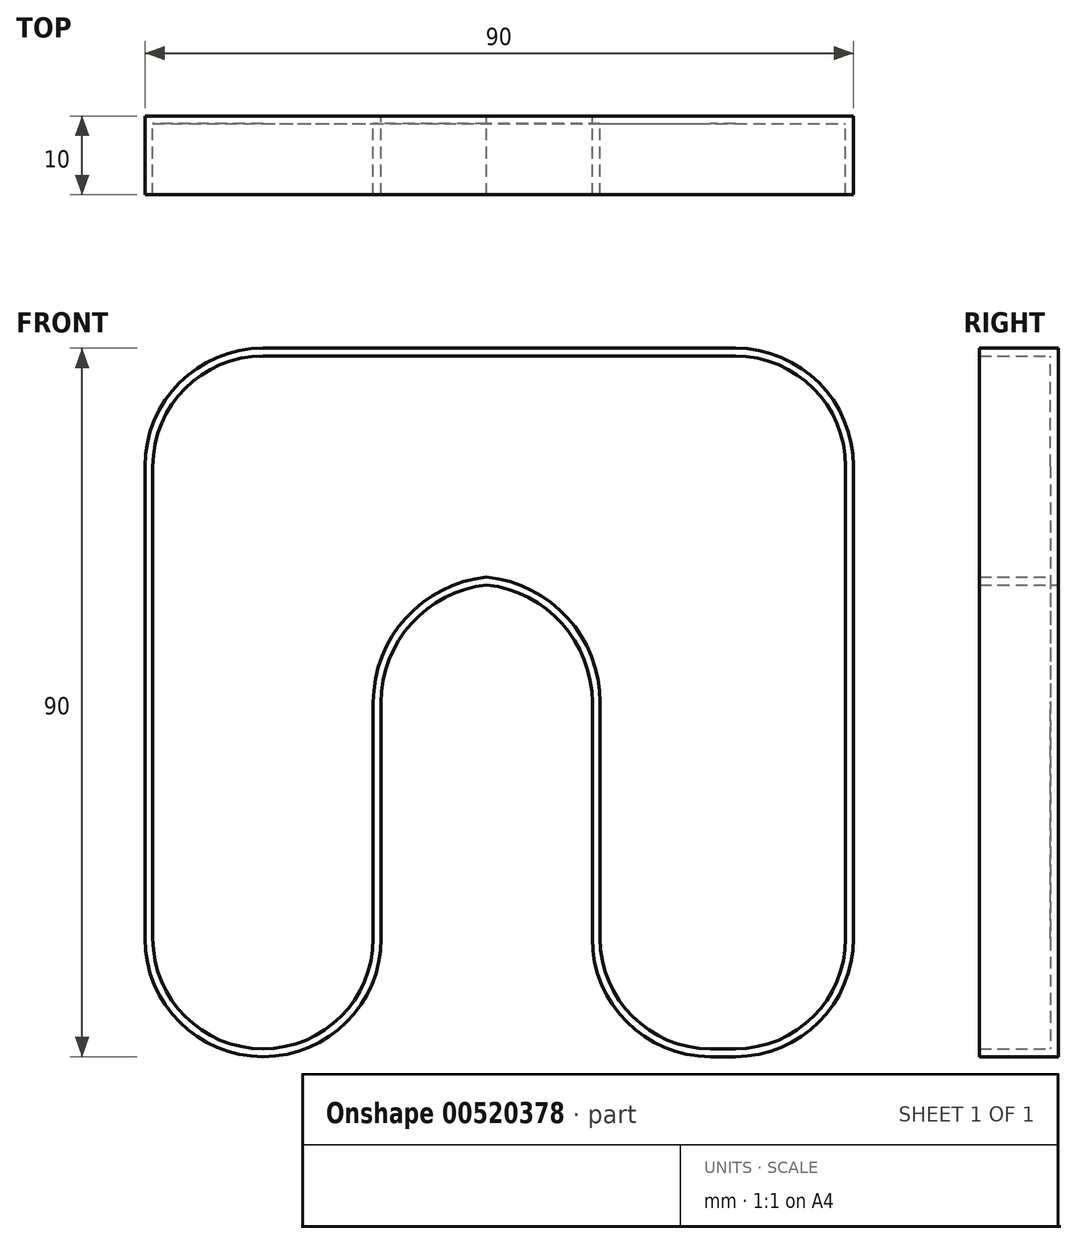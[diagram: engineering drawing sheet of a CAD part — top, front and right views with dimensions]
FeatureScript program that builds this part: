
annotation { "Feature Type Name" : "Feature", "Feature Type Description" : "" }
export const myFeature = defineFeature(function(context is Context, id is Id, definition is map)
    precondition{}
    {
        {
            var Q0;
            Q0=qCreatedBy(makeId("Front.planeOp"),FACE);
            var sketch = newSketch(context, id + "F0", { "sketchPlane" : qUnion([Q0])});
            skLineSegment(sketch, "E0", {"start": v(-141, 15) * mm, "end": v(-141, -45) * mm});
            skLineSegment(sketch, "E1", {"start": v(-126, 30) * mm, "end": v(-66, 30) * mm});
            skLineSegment(sketch, "E2", {"start": v(-51, 15) * mm, "end": v(-51, -45) * mm});
            skLineSegment(sketch, "E3", {"start": v(-66, -60) * mm, "end": v(-69.17, -60) * mm});
            skLineSegment(sketch, "E4", {"start": v(-84.17, -45) * mm, "end": v(-84.17, -15) * mm});
            skLineSegment(sketch, "E5", {"start": v(-96, 0) * mm, "end": v(-99.17, 0) * mm});
            skLineSegment(sketch, "E6", {"start": v(-111, -15) * mm, "end": v(-111, -45) * mm});
            skLineSegment(sketch, "E7", {"start": v(-126, -60) * mm, "end": v(-126, -60) * mm});
            skPoint(sketch, "E8.visualSharp", {"position": v(-141, 30) * mm});
            skArc(sketch, "E8.filletArc", {"start": v(-126, 30) * mm, "mid": v(-136.6, 25.6) * mm, "end": v(-141, 15) * mm});
            skPoint(sketch, "E9.visualSharp", {"position": v(-51, 30) * mm});
            skArc(sketch, "E9.filletArc", {"start": v(-51, 15) * mm, "mid": v(-55.39, 25.6) * mm, "end": v(-66, 30) * mm});
            skPoint(sketch, "E10.visualSharp", {"position": v(-51, -60) * mm});
            skArc(sketch, "E10.filletArc", {"start": v(-66, -60) * mm, "mid": v(-55.39, -55.6) * mm, "end": v(-51, -45) * mm});
            skPoint(sketch, "E11.visualSharp", {"position": v(-84.17, 0) * mm});
            skArc(sketch, "E11.filletArc", {"start": v(-84.17, -15) * mm, "mid": v(-88.56, -4.4) * mm, "end": v(-99.17, 0) * mm});
            skPoint(sketch, "E12.visualSharp", {"position": v(-84.17, -60) * mm});
            skArc(sketch, "E12.filletArc", {"start": v(-84.17, -45) * mm, "mid": v(-79.78, -55.6) * mm, "end": v(-69.17, -60) * mm});
            skPoint(sketch, "E13.visualSharp", {"position": v(-111, -60) * mm});
            skArc(sketch, "E13.filletArc", {"start": v(-126, -60) * mm, "mid": v(-115.39, -55.6) * mm, "end": v(-111, -45) * mm});
            skPoint(sketch, "E14.visualSharp", {"position": v(-111, 0) * mm});
            skArc(sketch, "E14.filletArc", {"start": v(-96, 0) * mm, "mid": v(-106.6, -4.4) * mm, "end": v(-111, -15) * mm});
            skPoint(sketch, "E15.visualSharp", {"position": v(-141, -60) * mm});
            skArc(sketch, "E15.filletArc", {"start": v(-141, -45) * mm, "mid": v(-136.6, -55.6) * mm, "end": v(-126, -60) * mm});
            skSolve(sketch);
        }
        {
            var Q0;
            {var subQ0=sQuery(id+"F0.wireOp",EDGE,"E5");Q0=makeQuery(id+"F0.imprint","IMPRINT",FACE,{"disambiguationData":[TD([[makeQuery(id+"F0.imprint","IMPRINT",EDGE,{"derivedFrom":subQ0}),1.0]])]});}
            var Q1;
            Q1=makeQuery(id+"F0.imprint","IMPRINT",FACE,{"disambiguationData":[TD([[makeQuery(id+"F0.imprint","IMPRINT",EDGE,{"derivedFrom":sQuery(id+"F0.wireOp",EDGE,"E0")}),1.0]])]});
            extrude(context, id + "F1", {"entities" : qUnion([Q0, Q1]), "depth" : 10 * mm, "offsetDistance" : 25 * mm});
        }
        {
            var Q0;
            Q0=makeQuery(id+"F1.opExtrude","CAP_FACE",FACE,{"disambiguationData":[OSD([sQuery(id+"F0.wireOp",EDGE,"E0"),sQuery(id+"F0.wireOp",EDGE,"E1"),sQuery(id+"F0.wireOp",EDGE,"E2"),sQuery(id+"F0.wireOp",EDGE,"E3"),sQuery(id+"F0.wireOp",EDGE,"E4"),sQuery(id+"F0.wireOp",EDGE,"E6"),sQuery(id+"F0.wireOp",EDGE,"E8.filletArc"),sQuery(id+"F0.wireOp",EDGE,"E9.filletArc"),sQuery(id+"F0.wireOp",EDGE,"E10.filletArc"),sQuery(id+"F0.wireOp",EDGE,"E11.filletArc"),sQuery(id+"F0.wireOp",EDGE,"E12.filletArc"),sQuery(id+"F0.wireOp",EDGE,"E13.filletArc"),sQuery(id+"F0.wireOp",EDGE,"E14.filletArc"),sQuery(id+"F0.wireOp",EDGE,"E15.filletArc")])],"isStart":false});
            shell(context, id + "F2", {"entities" : qUnion([Q0]), "thickness" : 1 * mm});
        }
    });
